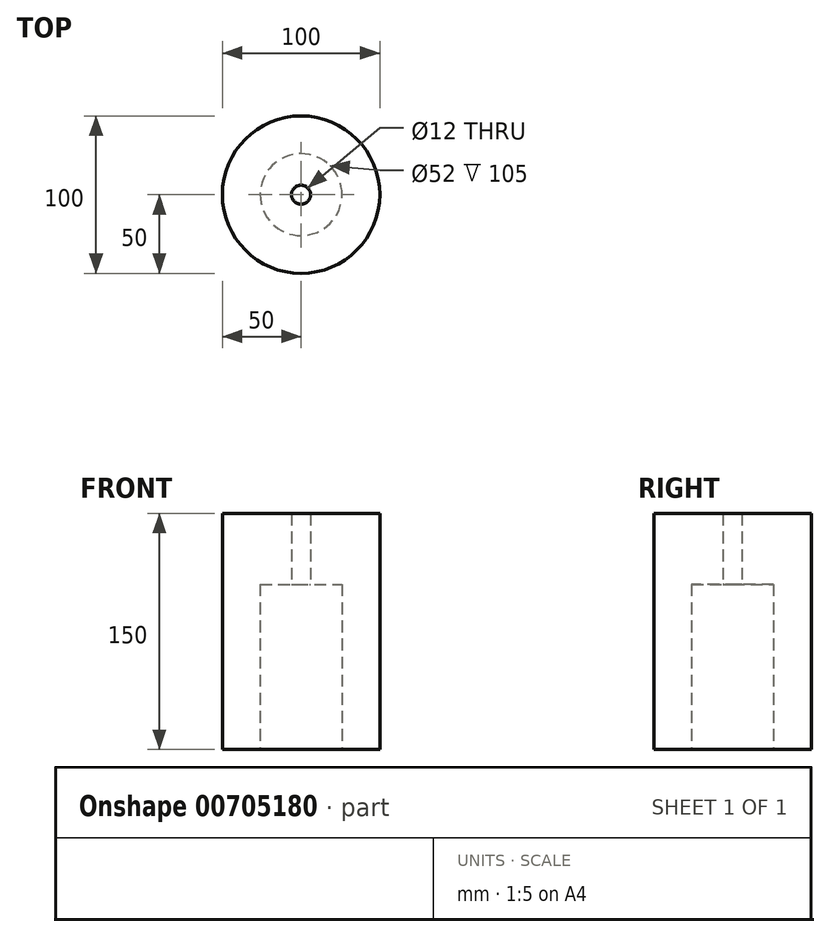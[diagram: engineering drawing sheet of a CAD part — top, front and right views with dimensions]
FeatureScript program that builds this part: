
annotation { "Feature Type Name" : "Feature", "Feature Type Description" : "" }
export const myFeature = defineFeature(function(context is Context, id is Id, definition is map)
    precondition{}
    {
        {
            var Q0;
            Q0=qCreatedBy(makeId("Front.planeOp"),FACE);
            var sketch = newSketch(context, id + "F0", { "sketchPlane" : qUnion([Q0])});
            skLineSegment(sketch, "E0.bottom", {"start": v(-6, 0) * mm, "end": v(-30, 0) * mm});
            skLineSegment(sketch, "E0.top", {"start": v(20, 150) * mm, "end": v(0, 150) * mm});
            skLineSegment(sketch, "E0.left", {"start": v(20, 105) * mm, "end": v(20, 150) * mm, "construction": true});
            skLineSegment(sketch, "E0.right", {"start": v(-30, 0) * mm, "end": v(-30, 150) * mm});
            skPoint(sketch, "E1.visualSharp", {"position": v(-30, 150) * mm});
            skLineSegment(sketch, "E2", {"start": v(-30, 150) * mm, "end": v(14, 150) * mm});
            skLineSegment(sketch, "E3.top", {"start": v(14, 105) * mm, "end": v(-6, 105) * mm});
            skLineSegment(sketch, "E3.right", {"start": v(-6, 0) * mm, "end": v(-6, 105) * mm});
            skLineSegment(sketch, "E4", {"start": v(14, 150) * mm, "end": v(14, 105) * mm});
            skSolve(sketch);
        }
        {
            var Q0;
            Q0=qSketchRegion(id+"F0",true);
            var Q1;
            Q1=sQuery(id+"F0.wireOp",EDGE,"E0.left");
            revolve(context, id + "F1", {"entities" : qUnion([Q0]), "axis" : qUnion([Q1]), "revolveType" : RevolveType.FULL});
        }
    });
